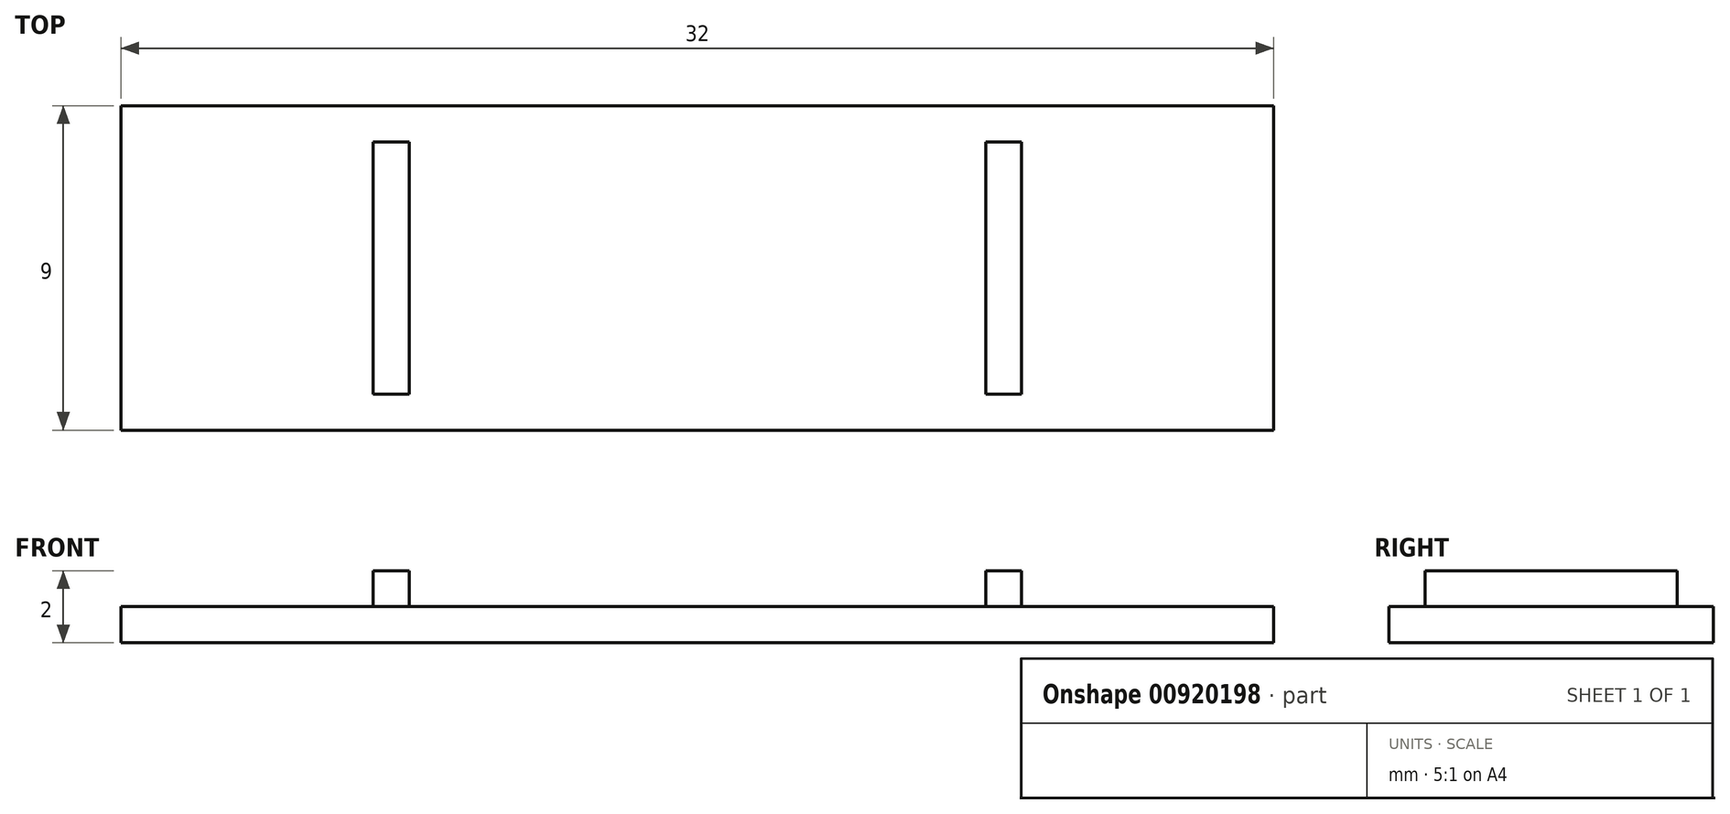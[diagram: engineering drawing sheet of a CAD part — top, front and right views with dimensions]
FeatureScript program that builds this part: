
annotation { "Feature Type Name" : "Feature", "Feature Type Description" : "" }
export const myFeature = defineFeature(function(context is Context, id is Id, definition is map)
    precondition{}
    {
        {
            var Q0;
            Q0=qCreatedBy(makeId("Front.planeOp"),FACE);
            var sketch = newSketch(context, id + "F0", { "sketchPlane" : qUnion([Q0])});
            skLineSegment(sketch, "E0.bottom", {"start": v(-16, 1) * mm, "end": v(16, 1) * mm});
            skLineSegment(sketch, "E0.top", {"start": v(-16, 0) * mm, "end": v(16, 0) * mm});
            skLineSegment(sketch, "E0.left", {"start": v(-16, 1) * mm, "end": v(-16, 0) * mm});
            skLineSegment(sketch, "E0.right", {"start": v(16, 1) * mm, "end": v(16, 0) * mm});
            skLineSegment(sketch, "E1.bottom", {"start": v(-9, 1) * mm, "end": v(-8, 1) * mm});
            skLineSegment(sketch, "E1.top", {"start": v(-9, 2) * mm, "end": v(-8, 2) * mm});
            skLineSegment(sketch, "E1.left", {"start": v(-9, 1) * mm, "end": v(-9, 2) * mm});
            skLineSegment(sketch, "E1.right", {"start": v(-8, 1) * mm, "end": v(-8, 2) * mm});
            skLineSegment(sketch, "E2.bottom", {"start": v(9, 1) * mm, "end": v(8, 1) * mm});
            skLineSegment(sketch, "E2.top", {"start": v(9, 2) * mm, "end": v(8, 2) * mm});
            skLineSegment(sketch, "E2.left", {"start": v(9, 1) * mm, "end": v(9, 2) * mm});
            skLineSegment(sketch, "E2.right", {"start": v(8, 1) * mm, "end": v(8, 2) * mm});
            skSolve(sketch);
        }
        {
            var Q0;
            Q0=makeQuery(id+"F0.imprint","IMPRINT",FACE,{"disambiguationData":[TD([[makeQuery(id+"F0.imprint","IMPRINT",EDGE,{"derivedFrom":sQuery(id+"F0.wireOp",EDGE,"E0.top")}),1.0]])]});
            var Q1;
            Q1=makeQuery(id+"F0.imprint","IMPRINT",FACE,{"disambiguationData":[TD([[makeQuery(id+"F0.imprint","IMPRINT",EDGE,{"derivedFrom":sQuery(id+"F0.wireOp",EDGE,"E1.top")}),-1.0]])]});
            var Q2;
            Q2=makeQuery(id+"F0.imprint","IMPRINT",FACE,{"disambiguationData":[TD([[makeQuery(id+"F0.imprint","IMPRINT",EDGE,{"derivedFrom":sQuery(id+"F0.wireOp",EDGE,"E2.top")}),1.0]])]});
            extrude(context, id + "F1", {"entities" : qUnion([Q0, Q1, Q2]), "depth" : 9 * mm, "offsetDistance" : 25 * mm});
        }
        {
            var Q0;
            Q0=makeQuery(id+"F1.opExtrude","CAP_FACE",FACE,{"disambiguationData":[OSD([sQuery(id+"F0.wireOp",EDGE,"E0.bottom"),sQuery(id+"F0.wireOp",EDGE,"E0.top"),sQuery(id+"F0.wireOp",EDGE,"E0.left"),sQuery(id+"F0.wireOp",EDGE,"E0.right"),sQuery(id+"F0.wireOp",EDGE,"E1.top"),sQuery(id+"F0.wireOp",EDGE,"E1.left"),sQuery(id+"F0.wireOp",EDGE,"E1.right"),sQuery(id+"F0.wireOp",EDGE,"E2.top"),sQuery(id+"F0.wireOp",EDGE,"E2.left"),sQuery(id+"F0.wireOp",EDGE,"E2.right")])],"isStart":false});
            var sketch = newSketch(context, id + "F2", { "sketchPlane" : qUnion([Q0])});
            skLineSegment(sketch, "E3.bottom", {"start": v(-9.91, 1) * mm, "end": v(10.03, 1) * mm});
            skLineSegment(sketch, "E3.top", {"start": v(-9.91, 3.15) * mm, "end": v(10.03, 3.15) * mm});
            skLineSegment(sketch, "E3.left", {"start": v(-9.91, 1) * mm, "end": v(-9.91, 3.15) * mm});
            skLineSegment(sketch, "E3.right", {"start": v(10.03, 1) * mm, "end": v(10.03, 3.15) * mm});
            skSolve(sketch);
        }
        {
            var Q0;
            Q0=makeQuery(id+"F2.imprint","IMPRINT",FACE,{"disambiguationData":[TD([[makeQuery(id+"F2.imprint","IMPRINT",EDGE,{"derivedFrom":sQuery(id+"F2.wireOp",EDGE,"E3.top")}),-1.0]])]});
            var Q1;
            Q1=makeQuery(id+"F2.imprint","IMPRINT",FACE,{"disambiguationData":[TD([[makeQuery(id+"F2.imprint","IMPRINT",EDGE,{"derivedFrom":makeQuery(id+"F1.opExtrude","CAP_EDGE",EDGE,{"disambiguationData":[OSD([sQuery(id+"F0.wireOp",EDGE,"E1.top")])],"isStart":false})}),-1.0]])]});
            var Q2;
            Q2=makeQuery(id+"F2.imprint","IMPRINT",FACE,{"disambiguationData":[TD([[makeQuery(id+"F2.imprint","IMPRINT",EDGE,{"derivedFrom":makeQuery(id+"F1.opExtrude","CAP_EDGE",EDGE,{"disambiguationData":[OSD([sQuery(id+"F0.wireOp",EDGE,"E2.top")])],"isStart":false})}),1.0]])]});
            extrude(context, id + "F3", {"entities" : qUnion([Q0, Q1, Q2]), "operationType" : NewBodyOperationType.REMOVE, "oppositeDirection" : true, "depth" : 1 * mm, "offsetDistance" : 25 * mm});
        }
        {
            var Q0;
            Q0=makeQuery(id+"F1.opExtrude","CAP_FACE",FACE,{"disambiguationData":[OSD([sQuery(id+"F0.wireOp",EDGE,"E0.bottom"),sQuery(id+"F0.wireOp",EDGE,"E0.top"),sQuery(id+"F0.wireOp",EDGE,"E0.left"),sQuery(id+"F0.wireOp",EDGE,"E0.right"),sQuery(id+"F0.wireOp",EDGE,"E1.top"),sQuery(id+"F0.wireOp",EDGE,"E1.left"),sQuery(id+"F0.wireOp",EDGE,"E1.right"),sQuery(id+"F0.wireOp",EDGE,"E2.top"),sQuery(id+"F0.wireOp",EDGE,"E2.left"),sQuery(id+"F0.wireOp",EDGE,"E2.right")])],"isStart":true});
            var sketch = newSketch(context, id + "F4", { "sketchPlane" : qUnion([Q0])});
            skLineSegment(sketch, "E4.bottom", {"start": v(-10.92, 2.63) * mm, "end": v(10.68, 2.63) * mm});
            skLineSegment(sketch, "E4.top", {"start": v(-10.92, 1) * mm, "end": v(10.68, 1) * mm});
            skLineSegment(sketch, "E4.left", {"start": v(-10.92, 2.63) * mm, "end": v(-10.92, 1) * mm});
            skLineSegment(sketch, "E4.right", {"start": v(10.68, 2.63) * mm, "end": v(10.68, 1) * mm});
            skSolve(sketch);
        }
        {
            var Q0;
            Q0=makeQuery(id+"F4.imprint","IMPRINT",FACE,{"disambiguationData":[TD([[makeQuery(id+"F4.imprint","IMPRINT",EDGE,{"derivedFrom":makeQuery(id+"F1.opExtrude","CAP_EDGE",EDGE,{"disambiguationData":[OSD([sQuery(id+"F0.wireOp",EDGE,"E2.top")])],"isStart":true})}),-1.0]])]});
            var Q1;
            Q1=makeQuery(id+"F4.imprint","IMPRINT",FACE,{"disambiguationData":[TD([[makeQuery(id+"F4.imprint","IMPRINT",EDGE,{"derivedFrom":makeQuery(id+"F1.opExtrude","CAP_EDGE",EDGE,{"disambiguationData":[OSD([sQuery(id+"F0.wireOp",EDGE,"E1.top")])],"isStart":true})}),1.0]])]});
            extrude(context, id + "F5", {"entities" : qUnion([Q0, Q1]), "operationType" : NewBodyOperationType.REMOVE, "oppositeDirection" : true, "depth" : 1 * mm, "offsetDistance" : 25 * mm});
        }
    });
